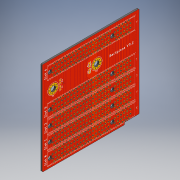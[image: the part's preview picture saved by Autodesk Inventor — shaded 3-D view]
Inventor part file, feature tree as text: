
AUTODESK INVENTOR PART (.ipt)
format: ipt  version: 2018 (Build 220112000, 112)  size: 1,380,864 bytes
history: native  units: mm
features: sketch x8, hole x5, other x4, extrude x1, fillet x1
ambient origin geometry x8: Origin, YZ Plane, XZ Plane, XY Plane, X Axis, Y Axis, Z Axis, Center Point
bodies: Body1 (feature_tree)
feature tree (19):
  extrude  "Extrusion3"  Depth=9.4mm
  fillet  "Fillet2"  Radius=82.8mm
  other  "Decal5"
  other  "Decal6"
  hole  "Hole7"  [1 undecoded]
  hole  "Hole8"  [1 undecoded]
  hole  "Hole9"  [1 undecoded]
  hole  "Hole12"  [1 undecoded]
  hole  "Hole13"  [1 undecoded]
  sketch  "Sketch11"  dims[d86=83.2mm d87=9.4mm d88=82.8mm]
  sketch  "Sketch14"  dims[d89=86.0mm d90=1.0mm d91=0.0mm]
  sketch  "Sketch15"  dims[d92=0.5mm]
  sketch  "Sketch16"  dims[d100=3.3mm d101=6.0mm d102=4.0mm d103=2.0mm d104=90.0deg d105=8.0mm d106=20.594885mm]
  sketch  "Sketch19"  dims[d107=2.35mm d108=6.0mm d109=4.0mm d110=2.0mm d111=90.0deg d112=8.0mm d113=20.594885mm]
  other  "Image9"
  sketch  "Sketch20"  dims[d114=0.7mm d115=6.0mm d116=4.0mm d117=2.0mm d118=90.0deg d119=8.0mm d120=20.594885mm d149=21.0mm]
  other  "Image10"
  sketch  "Sketch21"  dims[d150=17.0mm]
  sketch  "Sketch22"  dims[d163=0.45mm d164=6.0mm d165=4.0mm d166=2.0mm d167=90.0deg d168=8.0mm d169=20.594885mm d170=0.3mm d171=6.0mm d172=4.0mm d173=2.0mm d174=90.0deg d175=8.0mm d176=20.594885mm]
note: 5 required parameter values undecoded (feature->parameter linkage not recoverable at this tier; creation-order binding heuristic only, values carry confidence <= 0.55)
